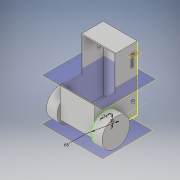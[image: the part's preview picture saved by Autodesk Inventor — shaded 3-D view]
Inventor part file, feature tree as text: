
AUTODESK INVENTOR PART (.ipt)
format: ipt  version: 2018 (Build 220112000, 112)  size: 209,408 bytes
history: native  units: mm
features: extrude x9, sketch x4, plane x3, mirror x2, other x1
ambient origin geometry x8: Origin, YZ Plane, XZ Plane, XY Plane, X Axis, Y Axis, Z Axis, Center Point
bodies: Body1 (feature_tree)
feature tree (19):
  other  "Sólido1"
  extrude  "Extrusión1"  Depth=150.0mm
  extrude  "Extrusión2"  Depth=50.0mm TaperAngle=0.0deg
  sketch  "Boceto2"  dims[d0=80.0mm d1=150.0mm]
  extrude  "Extrusión3"  Depth=65.0mm
  extrude  "Extrusión4"  Depth=30.0mm
  mirror  "Simetría1"
  sketch  "Boceto3"  dims[d2=2.5mm d3=50.0mm d4=0.0mm]
  extrude  "Extrusión5"  Depth=10.0mm TaperAngle=0.0deg
  extrude  "Extrusión6"  Depth=25.0mm TaperAngle=0.0deg
  extrude  "Extrusión7"  Depth=50.0mm
  plane  "Plano de trabajo1"
  sketch  "Boceto4"  dims[d5=0.5mm d6=0.0mm d9=65.0mm]
  plane  "Plano de trabajo2"
  extrude  "Extrusión8"  Depth=80.0mm
  plane  "Plano de trabajo3"
  mirror  "Simetría2"
  extrude  "Extrusión9"  Depth=47.5mm
  sketch  "Boceto5"  dims[d15=24.0mm d16=30.0mm d18=10.0mm d19=0.0mm d20=25.0mm d21=0.0mm d24=50.0mm d25=80.0mm d26=47.5mm d27=75.0mm d28=70.0mm d29=0.0mm d30=0.5mm d31=0.0mm d32=0.5mm d35=80.0mm d36=0.0mm d39=100.0mm d40=2.0mm d41=6.0mm d42=5.0mm d43=0.0mm d44=90.0deg d45=24.0mm d46=10.0mm d47=8.0mm d49=20.0mm d50=5.0mm d51=0.0mm d53=6.0mm]
